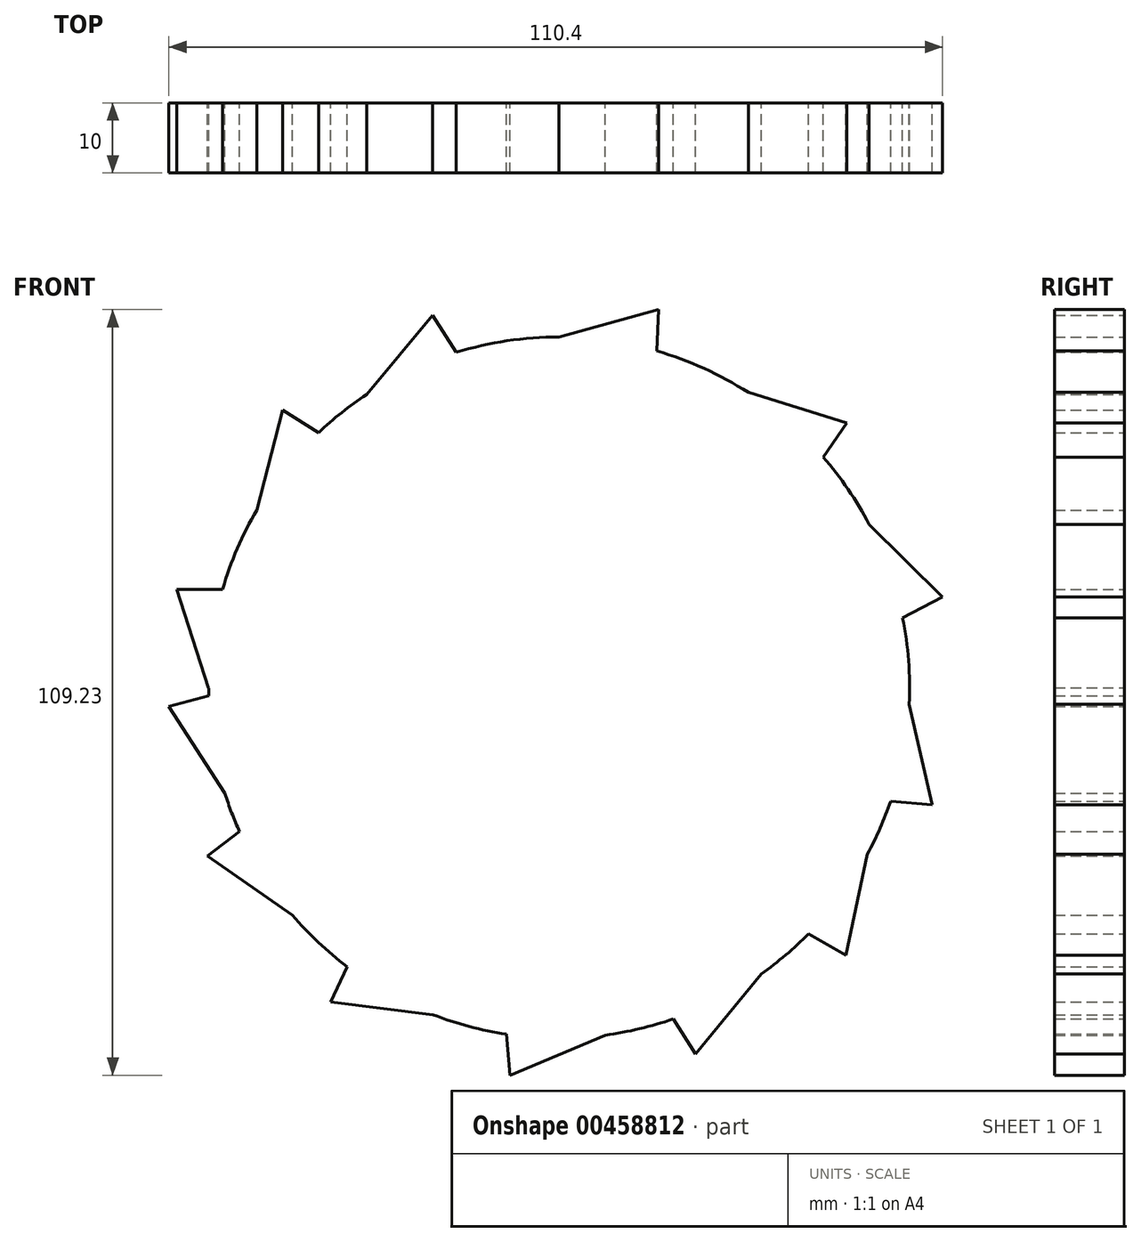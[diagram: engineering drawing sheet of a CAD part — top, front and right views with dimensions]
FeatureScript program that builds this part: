
annotation { "Feature Type Name" : "Feature", "Feature Type Description" : "" }
export const myFeature = defineFeature(function(context is Context, id is Id, definition is map)
    precondition{}
    {
        {
            var Q0;
            Q0=qCreatedBy(makeId("Front.planeOp"),FACE);
            var sketch = newSketch(context, id + "F0", { "sketchPlane" : qUnion([Q0])});
            skCircle(sketch, "E0", {"center": v(0, 0) * mm, "radius": 50.02 * mm});
            skLineSegment(sketch, "E1", {"start": v(-50.02, 0) * mm, "end": v(-54.54, 14.04) * mm});
            skLineSegment(sketch, "E2", {"start": v(-54.54, 14.04) * mm, "end": v(-48.01, 14.04) * mm});
            skLineSegment(sketch, "E3", {"start": v(-27.47, 41.8) * mm, "end": v(-18.03, 53.13) * mm});
            skLineSegment(sketch, "E4", {"start": v(-18.03, 53.13) * mm, "end": v(-14.54, 47.62) * mm});
            skLineSegment(sketch, "E5", {"start": v(-43.14, 25.33) * mm, "end": v(-39.46, 39.61) * mm});
            skLineSegment(sketch, "E6", {"start": v(-39.46, 39.61) * mm, "end": v(-33.94, 36.13) * mm});
            skLineSegment(sketch, "E7", {"start": v(0, 50.02) * mm, "end": v(14.22, 53.92) * mm});
            skLineSegment(sketch, "E8", {"start": v(14.22, 53.92) * mm, "end": v(13.94, 47.4) * mm});
            skLineSegment(sketch, "E9", {"start": v(27, 42.1) * mm, "end": v(41.1, 37.75) * mm});
            skLineSegment(sketch, "E10", {"start": v(41.1, 37.75) * mm, "end": v(37.35, 32.4) * mm});
            skLineSegment(sketch, "E11", {"start": v(44.27, 23.3) * mm, "end": v(54.72, 12.9) * mm});
            skLineSegment(sketch, "E12", {"start": v(54.72, 12.9) * mm, "end": v(48.93, 9.9) * mm});
            skLineSegment(sketch, "E13", {"start": v(49.97, -2.35) * mm, "end": v(53.24, -16.73) * mm});
            skLineSegment(sketch, "E14", {"start": v(53.24, -16.73) * mm, "end": v(46.74, -16.16) * mm});
            skLineSegment(sketch, "E15", {"start": v(44.02, -23.76) * mm, "end": v(40.91, -38.18) * mm});
            skLineSegment(sketch, "E16", {"start": v(40.91, -38.18) * mm, "end": v(35.26, -34.91) * mm});
            skLineSegment(sketch, "E17", {"start": v(28.85, -40.86) * mm, "end": v(19.5, -52.26) * mm});
            skLineSegment(sketch, "E18", {"start": v(19.5, -52.26) * mm, "end": v(15.96, -46.77) * mm});
            skLineSegment(sketch, "E19", {"start": v(6.58, -49.59) * mm, "end": v(-7, -55.3) * mm});
            skLineSegment(sketch, "E20", {"start": v(-7, -55.3) * mm, "end": v(-7.57, -48.81) * mm});
            skLineSegment(sketch, "E21", {"start": v(-17.97, -46.68) * mm, "end": v(-32.6, -44.84) * mm});
            skLineSegment(sketch, "E22", {"start": v(-32.6, -44.84) * mm, "end": v(-29.85, -38.93) * mm});
            skLineSegment(sketch, "E23", {"start": v(-38.06, -32.46) * mm, "end": v(-50.16, -24.04) * mm});
            skLineSegment(sketch, "E24", {"start": v(-50.16, -24.04) * mm, "end": v(-44.97, -20.09) * mm});
            skLineSegment(sketch, "E25", {"start": v(-47.69, -15.1) * mm, "end": v(-55.68, -2.72) * mm});
            skLineSegment(sketch, "E26", {"start": v(-55.68, -2.72) * mm, "end": v(-49.38, -1.03) * mm});
            skSolve(sketch);
        }
        {
            var Q0;
            Q0 = qSketchRegion(id + "F0", true);
            extrude(context, id + "F1", {"entities" : qUnion([Q0]), "depth" : 10 * mm, "offsetDistance" : 25 * mm});
        }
    });
